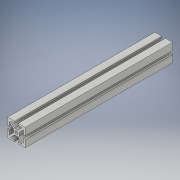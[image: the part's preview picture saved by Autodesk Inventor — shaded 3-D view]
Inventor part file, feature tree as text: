
AUTODESK INVENTOR PART (.ipt)
format: ipt  version: 2018 (Build 220112000, 112)  size: 154,112 bytes
history: native  units: mm
features: extrude x1, sketch x1
ambient origin geometry x8: Origin, YZ Plane, XZ Plane, XY Plane, X Axis, Y Axis, Z Axis, Center Point
bodies: Volumenkörper1 (feature_tree)
feature tree (2):
  extrude  "Extrusion1"  Depth=3.0mm
  sketch  "Skizze1"  dims[d0=3.0mm d1=3.0mm d2=0.5mm d3=1.0mm d4=1.0mm d5=1.2mm d6=1.2mm d7=1.2mm d8=1.2mm d9=0.3mm d10=0.15mm d11=0.15mm d12=0.15mm d13=0.15mm d14=25.0mm d15=0.0mm]
